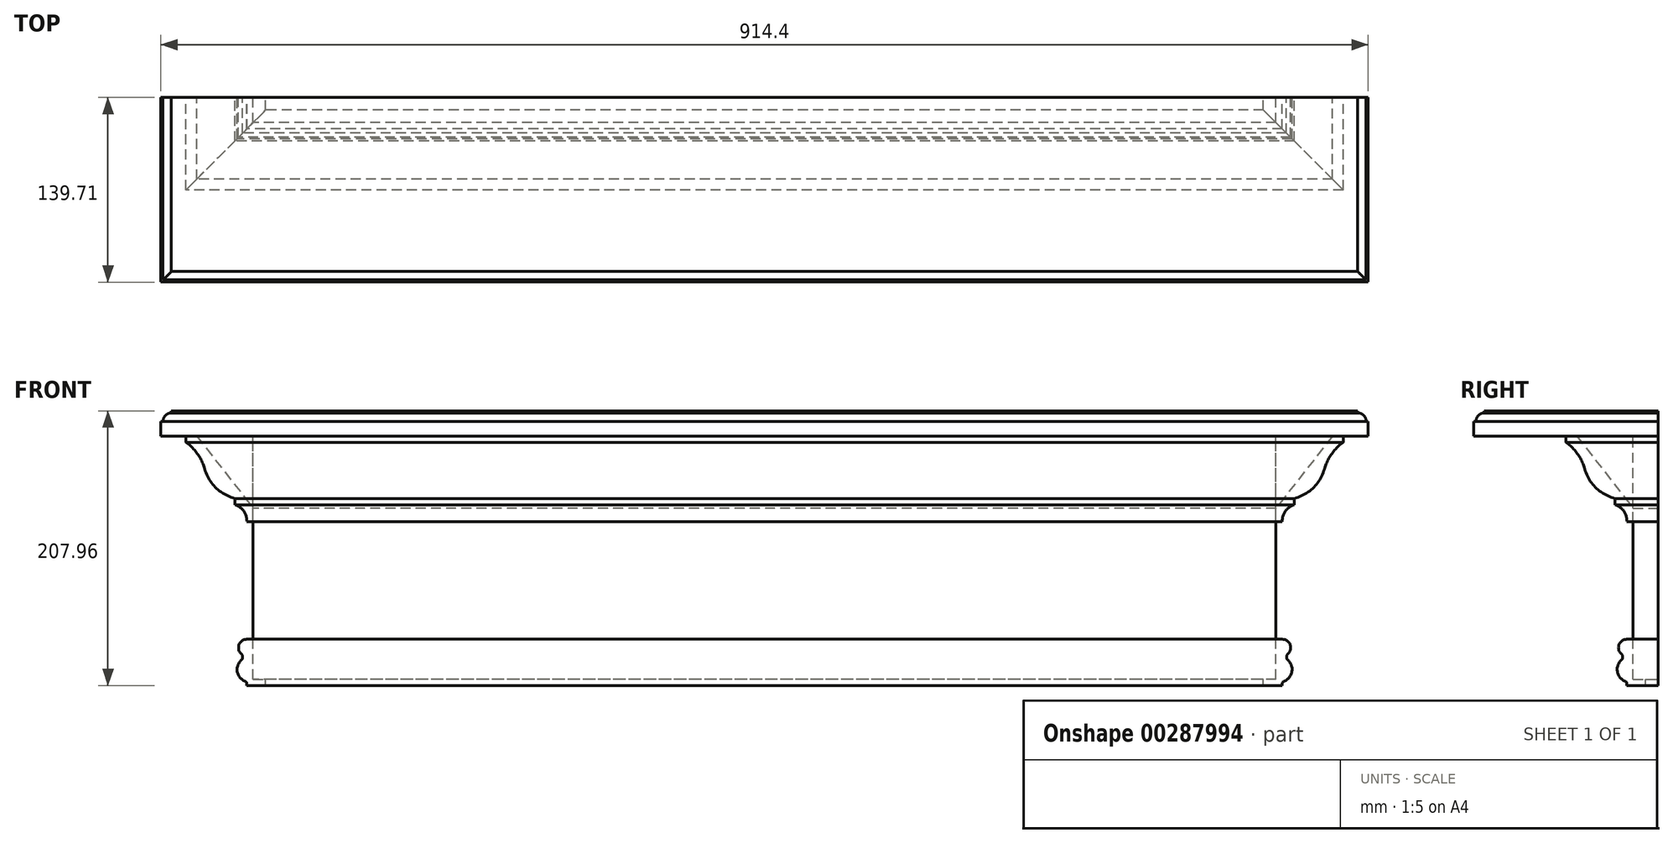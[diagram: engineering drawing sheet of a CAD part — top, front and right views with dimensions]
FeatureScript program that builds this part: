
annotation { "Feature Type Name" : "Feature", "Feature Type Description" : "" }
export const myFeature = defineFeature(function(context is Context, id is Id, definition is map)
    precondition{}
    {
        {
            var Q0;
            Q0=qCreatedBy(makeId("Right.planeOp"),FACE);
            var sketch = newSketch(context, id + "F0", { "sketchPlane" : qUnion([Q0])});
            skLineSegment(sketch, "E0.bottom", {"start": v(-9.52, -92.08) * mm, "end": v(9.52, -92.08) * mm});
            skLineSegment(sketch, "E0.top", {"start": v(-9.52, 92.08) * mm, "end": v(9.52, 92.08) * mm});
            skLineSegment(sketch, "E0.left", {"start": v(-9.52, -92.07) * mm, "end": v(-9.52, 92.08) * mm});
            skLineSegment(sketch, "E0.right", {"start": v(9.52, -92.07) * mm, "end": v(9.52, 92.08) * mm});
            skPoint(sketch, "E0.middle", {"position": v(0, 0) * mm});
            skLineSegment(sketch, "E1.bottom", {"start": v(9.52, 92.08) * mm, "end": v(-130.18, 92.08) * mm});
            skLineSegment(sketch, "E1.top", {"start": v(9.53, 111.13) * mm, "end": v(-130.18, 111.12) * mm});
            skLineSegment(sketch, "E1.left", {"start": v(9.53, 92.08) * mm, "end": v(9.53, 111.13) * mm});
            skLineSegment(sketch, "E1.right", {"start": v(-130.18, 92.08) * mm, "end": v(-130.18, 111.12) * mm});
            skLineSegment(sketch, "E2", {"start": v(-52.29, 92.08) * mm, "end": v(-9.52, 37.34) * mm});
            skLineSegment(sketch, "E3", {"start": v(-9.52, 27.02) * mm, "end": v(-60.35, 92.08) * mm, "construction": true});
            skLineSegment(sketch, "E4", {"start": v(-9.52, 27.02) * mm, "end": v(-14.29, 27.02) * mm});
            skArc(sketch, "E5", {"start": v(-14.29, 27.02) * mm, "mid": v(-16.56, 35.12) * mm, "end": v(-23.4, 40.02) * mm});
            skLineSegment(sketch, "E6", {"start": v(-23.4, 40.02) * mm, "end": v(-23.4, 44.79) * mm});
            skArc(sketch, "E7", {"start": v(-46.16, 66.92) * mm, "mid": v(-37.75, 52.8) * mm, "end": v(-23.4, 44.79) * mm});
            skArc(sketch, "E8", {"start": v(-46.16, 66.92) * mm, "mid": v(-51.55, 78.3) * mm, "end": v(-60.35, 87.31) * mm});
            skLineSegment(sketch, "E9", {"start": v(-60.35, 87.31) * mm, "end": v(-60.35, 92.08) * mm});
            skLineSegment(sketch, "E10", {"start": v(-9.52, -61.86) * mm, "end": v(-14.29, -61.86) * mm});
            skArc(sketch, "E11", {"start": v(-14.29, -61.86) * mm, "mid": v(-20.22, -65.94) * mm, "end": v(-18.52, -72.94) * mm});
            skArc(sketch, "E12", {"start": v(-18.52, -77.67) * mm, "mid": v(-17.46, -75.3) * mm, "end": v(-18.52, -72.94) * mm});
            skArc(sketch, "E13", {"start": v(-18.52, -77.67) * mm, "mid": v(-21.52, -86.62) * mm, "end": v(-15.35, -93.75) * mm});
            skLineSegment(sketch, "E14", {"start": v(0, -96.84) * mm, "end": v(0, -92.08) * mm});
            skLineSegment(sketch, "E15", {"start": v(-14.29, -95.25) * mm, "end": v(-14.29, -96.84) * mm});
            skLineSegment(sketch, "E16", {"start": v(-14.29, -96.84) * mm, "end": v(0, -96.84) * mm});
            skPoint(sketch, "E17.visualSharp", {"position": v(-14.29, -94.06) * mm});
            skArc(sketch, "E17.filletArc", {"start": v(-14.29, -95.25) * mm, "mid": v(-14.58, -94.33) * mm, "end": v(-15.35, -93.75) * mm});
            skLineSegment(sketch, "E18", {"start": v(-122.24, 111.12) * mm, "end": v(-122.24, 109.54) * mm});
            skArc(sketch, "E19", {"start": v(-122.24, 109.54) * mm, "mid": v(-126.73, 107.68) * mm, "end": v(-128.59, 103.19) * mm});
            skLineSegment(sketch, "E20", {"start": v(-128.59, 103.19) * mm, "end": v(-130.17, 103.19) * mm});
            skSolve(sketch);
        }
        {
            var Q0;
            Q0=qCreatedBy(makeId("Front.planeOp"),FACE);
            var sketch = newSketch(context, id + "F1", { "sketchPlane" : qUnion([Q0])});
            skLineSegment(sketch, "E21", {"start": v(-387.35, 0) * mm, "end": v(387.35, 0) * mm});
            skLineSegment(sketch, "E22", {"start": v(-387.35, 0) * mm, "end": v(-457.2, 0) * mm});
            skLineSegment(sketch, "E23", {"start": v(387.35, 0) * mm, "end": v(457.2, 0) * mm});
            skSolve(sketch);
        }
        {
            var Q0;
            {var subQ7=sQuery(id+"F0.wireOp",EDGE,"E1.left");Q0=makeQuery(id+"F0.imprint","IMPRINT",FACE,{"disambiguationData":[TD([[makeQuery(id+"F0.imprint","IMPRINT",EDGE,{"derivedFrom":subQ7}),1.0]])]});}
            var Q1;
            Q1=sQuery(id+"F1.wireOp",VERTEX,"E23.end");
            extrude(context, id + "F2", {"entities" : qUnion([Q0]), "endBound" : BoundingType.UP_TO_VERTEX, "endBoundEntityVertex" : qUnion([Q1]), "depth" : 25.4 * mm});
        }
        {
            var Q0;
            Q0=makeQuery(id+"F2.opExtrude","SWEPT_FACE",FACE,{"disambiguationData":[OSD([sQuery(id+"F0.wireOp",EDGE,"E1.left")])]});
            var sketch = newSketch(context, id + "F3", { "sketchPlane" : qUnion([Q0])});
            skLineSegment(sketch, "E24", {"start": v(-449.26, 111.13) * mm, "end": v(-449.26, 109.54) * mm});
            skLineSegment(sketch, "E25", {"start": v(-457.2, 103.19) * mm, "end": v(-455.61, 103.19) * mm});
            skArc(sketch, "E26", {"start": v(-449.26, 109.54) * mm, "mid": v(-453.75, 107.68) * mm, "end": v(-455.61, 103.19) * mm});
            skLineSegment(sketch, "E27", {"start": v(-457.2, 103.19) * mm, "end": v(-457.2, 111.13) * mm});
            skLineSegment(sketch, "E28", {"start": v(-457.2, 111.13) * mm, "end": v(-449.26, 111.13) * mm});
            skSolve(sketch);
        }
        {
            var Q0;
            Q0 = qSketchRegion(id + "F3", true);
            extrude(context, id + "F4", {"entities" : qUnion([Q0]), "operationType" : NewBodyOperationType.REMOVE, "endBound" : BoundingType.THROUGH_ALL, "oppositeDirection" : true, "depth" : 25.4 * mm});
        }
        {
            var Q0;
            Q0=makeQuery(id+"F2.opExtrude","SWEPT_BODY",BODY,{"disambiguationData":[OSD([sQuery(id+"F0.wireOp",EDGE,"E1.bottom"),sQuery(id+"F0.wireOp",EDGE,"E1.top"),sQuery(id+"F0.wireOp",EDGE,"E1.left"),sQuery(id+"F0.wireOp",EDGE,"E1.right"),sQuery(id+"F0.wireOp",EDGE,"E18"),sQuery(id+"F0.wireOp",EDGE,"E19"),sQuery(id+"F0.wireOp",EDGE,"E20")])]});
            var Q1;
            Q1=qCreatedBy(makeId("Right.planeOp"),FACE);
            mirror(context, id + "F5", {"operationType" : NewBodyOperationType.ADD, "entities" : qUnion([Q0]), "mirrorPlane" : qUnion([Q1])});
        }
        {
            var Q0;
            {var subQ5=sQuery(id+"F0.wireOp",EDGE,"E0.bottom");Q0=makeQuery(id+"F0.imprint","IMPRINT",FACE,{"disambiguationData":[TD([[makeQuery(id+"F0.imprint","IMPRINT",EDGE,{"derivedFrom":subQ5}),1.0]])]});}
            var Q1;
            Q1=sQuery(id+"F1.wireOp",VERTEX,"E23.start");
            extrude(context, id + "F6", {"entities" : qUnion([Q0]), "endBound" : BoundingType.UP_TO_VERTEX, "endBoundEntityVertex" : qUnion([Q1]), "depth" : 25.4 * mm});
        }
        {
            var Q0;
            Q0=makeQuery(id+"F6.opExtrude","SWEPT_BODY",BODY,{"disambiguationData":[OSD([sQuery(id+"F0.wireOp",EDGE,"E0.bottom"),sQuery(id+"F0.wireOp",EDGE,"E0.left"),sQuery(id+"F0.wireOp",EDGE,"E0.right"),sQuery(id+"F0.wireOp",EDGE,"E1.bottom")])]});
            var Q1;
            Q1=qCreatedBy(makeId("Right.planeOp"),FACE);
            mirror(context, id + "F7", {"operationType" : NewBodyOperationType.ADD, "entities" : qUnion([Q0]), "mirrorPlane" : qUnion([Q1])});
        }
        {
            var Q0;
            {var subQ0=sQuery(id+"F0.wireOp",EDGE,"E2");Q0=makeQuery(id+"F0.imprint","IMPRINT",FACE,{"disambiguationData":[TD([[makeQuery(id+"F0.imprint","IMPRINT",EDGE,{"derivedFrom":subQ0}),-1.0]])]});}
            var Q1;
            Q1=sQuery(id+"F1.wireOp",VERTEX,"E23.end");
            extrude(context, id + "F8", {"entities" : qUnion([Q0]), "endBound" : BoundingType.UP_TO_VERTEX, "endBoundEntityVertex" : qUnion([Q1]), "depth" : 25.4 * mm});
        }
        {
            var Q0;
            Q0=makeQuery(id+"F6.opExtrude","CAP_EDGE",EDGE,{"disambiguationData":[OSD([sQuery(id+"F0.wireOp",EDGE,"E0.left")])],"isStart":false});
            var Q1;
            Q1=makeQuery(id+"F6.opExtrude","CAP_FACE",FACE,{"disambiguationData":[OSD([sQuery(id+"F0.wireOp",EDGE,"E0.bottom"),sQuery(id+"F0.wireOp",EDGE,"E0.left"),sQuery(id+"F0.wireOp",EDGE,"E0.right"),sQuery(id+"F0.wireOp",EDGE,"E1.bottom")])],"isStart":false});
            cPlane(context, id + "F9", {"entities" : qUnion([Q0, Q1]), "cplaneType" : CPlaneType.LINE_ANGLE, "offset" : 25.4 * mm, "angle" : 45 * degree, "width" : 152.4 * mm, "height" : 152.4 * mm});
        }
        {
            var Q0;
            Q0=makeQuery(id+"F8.opExtrude","CAP_FACE",FACE,{"disambiguationData":[OSD([sQuery(id+"F0.wireOp",EDGE,"E0.left"),sQuery(id+"F0.wireOp",EDGE,"E1.bottom"),sQuery(id+"F0.wireOp",EDGE,"E2"),sQuery(id+"F0.wireOp",EDGE,"E4"),sQuery(id+"F0.wireOp",EDGE,"E5"),sQuery(id+"F0.wireOp",EDGE,"E6"),sQuery(id+"F0.wireOp",EDGE,"E7"),sQuery(id+"F0.wireOp",EDGE,"E8"),sQuery(id+"F0.wireOp",EDGE,"E9")])],"isStart":false});
            var Q1;
            Q1=qCreatedBy(id+"F9.planeOp",FACE);
            extrude(context, id + "F10", {"entities" : qUnion([Q0]), "operationType" : NewBodyOperationType.REMOVE, "endBound" : BoundingType.UP_TO_SURFACE, "oppositeDirection" : true, "endBoundEntityFace" : qUnion([Q1]), "depth" : 25.4 * mm});
        }
        {
            var Q0;
            Q0=makeQuery(id+"F8.opExtrude","SWEPT_BODY",BODY,{"disambiguationData":[OSD([sQuery(id+"F0.wireOp",EDGE,"E0.left"),sQuery(id+"F0.wireOp",EDGE,"E1.bottom"),sQuery(id+"F0.wireOp",EDGE,"E2"),sQuery(id+"F0.wireOp",EDGE,"E4"),sQuery(id+"F0.wireOp",EDGE,"E5"),sQuery(id+"F0.wireOp",EDGE,"E6"),sQuery(id+"F0.wireOp",EDGE,"E7"),sQuery(id+"F0.wireOp",EDGE,"E8"),sQuery(id+"F0.wireOp",EDGE,"E9")])]});
            var Q1;
            Q1=qCreatedBy(makeId("Right.planeOp"),FACE);
            mirror(context, id + "F11", {"operationType" : NewBodyOperationType.ADD, "entities" : qUnion([Q0]), "mirrorPlane" : qUnion([Q1])});
        }
        {
            var Q0;
            {var subQ0=makeQuery(id+"F6.opExtrude","SWEPT_FACE",FACE,{"disambiguationData":[OSD([sQuery(id+"F0.wireOp",EDGE,"E0.right")])]});Q0=makeQuery(id+"F7.boolean.opBoolean","MERGE",FACE,{"derivedFrom":[subQ0,makeQuery(id+"F7.opPattern","COPY",FACE,{"derivedFrom":subQ0,"instanceName":"1"})]});}
            var sketch = newSketch(context, id + "F12", { "sketchPlane" : qUnion([Q0])});
            skLineSegment(sketch, "E29.0", {"start": v(-430.11, 92.07) * mm, "end": v(-387.35, 37.34) * mm});
            skLineSegment(sketch, "E30.0", {"start": v(-438.17, 87.31) * mm, "end": v(-438.17, 92.08) * mm});
            skArc(sketch, "E31.0", {"start": v(-423.99, 66.92) * mm, "mid": v(-429.37, 78.3) * mm, "end": v(-438.17, 87.31) * mm});
            skArc(sketch, "E32.0", {"start": v(-423.99, 66.92) * mm, "mid": v(-415.57, 52.8) * mm, "end": v(-401.23, 44.79) * mm});
            skLineSegment(sketch, "E33.0", {"start": v(-401.23, 40.02) * mm, "end": v(-401.23, 44.79) * mm});
            skArc(sketch, "E34.0", {"start": v(-392.11, 27.02) * mm, "mid": v(-394.39, 35.12) * mm, "end": v(-401.23, 40.02) * mm});
            skLineSegment(sketch, "E35.0", {"start": v(-387.35, 27.02) * mm, "end": v(-392.11, 27.02) * mm});
            skLineSegment(sketch, "E36", {"start": v(-387.35, 27.02) * mm, "end": v(-387.35, 37.34) * mm});
            skLineSegment(sketch, "E37", {"start": v(-438.17, 92.08) * mm, "end": v(-430.11, 92.08) * mm});
            skSolve(sketch);
        }
        {
            var Q0;
            Q0 = qSketchRegion(id + "F12", true);
            var Q1;
            Q1=makeQuery(id+"F10.boolean.opBoolean","COPY",FACE,{"derivedFrom":makeQuery(id+"F10.opExtrude","CAP_FACE",FACE,{"disambiguationData":[OSD([sQuery(id+"F0.wireOp",EDGE,"E0.left"),sQuery(id+"F0.wireOp",EDGE,"E1.bottom"),sQuery(id+"F0.wireOp",EDGE,"E2"),sQuery(id+"F0.wireOp",EDGE,"E4"),sQuery(id+"F0.wireOp",EDGE,"E5"),sQuery(id+"F0.wireOp",EDGE,"E6"),sQuery(id+"F0.wireOp",EDGE,"E7"),sQuery(id+"F0.wireOp",EDGE,"E8"),sQuery(id+"F0.wireOp",EDGE,"E9")])],"isStart":false})});
            extrude(context, id + "F13", {"entities" : qUnion([Q0]), "endBound" : BoundingType.UP_TO_SURFACE, "oppositeDirection" : true, "endBoundEntityFace" : qUnion([Q1]), "depth" : 25.4 * mm});
        }
        {
            var Q0;
            {var subQ0=sQuery(id+"F0.wireOp",EDGE,"E10");Q0=makeQuery(id+"F0.imprint","IMPRINT",FACE,{"disambiguationData":[TD([[makeQuery(id+"F0.imprint","IMPRINT",EDGE,{"derivedFrom":subQ0}),1.0]])]});}
            var Q1;
            Q1=makeQuery(id+"F6.opExtrude","CAP_FACE",FACE,{"disambiguationData":[OSD([sQuery(id+"F0.wireOp",EDGE,"E0.bottom"),sQuery(id+"F0.wireOp",EDGE,"E0.left"),sQuery(id+"F0.wireOp",EDGE,"E0.right"),sQuery(id+"F0.wireOp",EDGE,"E1.bottom")])],"isStart":false});
            var Q2;
            Q2=sQuery(id+"F1.wireOp",VERTEX,"E23.end");
            extrude(context, id + "F14", {"entities" : qUnion([Q0]), "endBound" : BoundingType.UP_TO_VERTEX, "endBoundEntityFace" : qUnion([Q1]), "endBoundEntityVertex" : qUnion([Q2]), "depth" : 25.4 * mm});
        }
        {
            var Q0;
            Q0=makeQuery(id+"F14.opExtrude","CAP_FACE",FACE,{"disambiguationData":[OSD([sQuery(id+"F0.wireOp",EDGE,"E0.bottom"),sQuery(id+"F0.wireOp",EDGE,"E0.left"),sQuery(id+"F0.wireOp",EDGE,"E10"),sQuery(id+"F0.wireOp",EDGE,"E11"),sQuery(id+"F0.wireOp",EDGE,"E12"),sQuery(id+"F0.wireOp",EDGE,"E13"),sQuery(id+"F0.wireOp",EDGE,"E14"),sQuery(id+"F0.wireOp",EDGE,"E15"),sQuery(id+"F0.wireOp",EDGE,"E16"),sQuery(id+"F0.wireOp",EDGE,"E17.filletArc")])],"isStart":false});
            var Q1;
            Q1=qCreatedBy(id+"F9.planeOp",FACE);
            extrude(context, id + "F15", {"entities" : qUnion([Q0]), "operationType" : NewBodyOperationType.REMOVE, "endBound" : BoundingType.UP_TO_SURFACE, "oppositeDirection" : true, "endBoundEntityFace" : qUnion([Q1]), "depth" : 25.4 * mm});
        }
        {
            var Q0;
            Q0=makeQuery(id+"F14.opExtrude","SWEPT_BODY",BODY,{"disambiguationData":[OSD([sQuery(id+"F0.wireOp",EDGE,"E0.bottom"),sQuery(id+"F0.wireOp",EDGE,"E0.left"),sQuery(id+"F0.wireOp",EDGE,"E10"),sQuery(id+"F0.wireOp",EDGE,"E11"),sQuery(id+"F0.wireOp",EDGE,"E12"),sQuery(id+"F0.wireOp",EDGE,"E13"),sQuery(id+"F0.wireOp",EDGE,"E14"),sQuery(id+"F0.wireOp",EDGE,"E15"),sQuery(id+"F0.wireOp",EDGE,"E16"),sQuery(id+"F0.wireOp",EDGE,"E17.filletArc")])]});
            var Q1;
            Q1=qCreatedBy(makeId("Right.planeOp"),FACE);
            mirror(context, id + "F16", {"operationType" : NewBodyOperationType.ADD, "entities" : qUnion([Q0]), "mirrorPlane" : qUnion([Q1])});
        }
        {
            var Q0;
            {var subQ0=makeQuery(id+"F6.opExtrude","SWEPT_FACE",FACE,{"disambiguationData":[OSD([sQuery(id+"F0.wireOp",EDGE,"E0.right")])]});Q0=makeQuery(id+"F7.boolean.opBoolean","MERGE",FACE,{"derivedFrom":[subQ0,makeQuery(id+"F7.opPattern","COPY",FACE,{"derivedFrom":subQ0,"instanceName":"1"})]});}
            var sketch = newSketch(context, id + "F17", { "sketchPlane" : qUnion([Q0])});
            skLineSegment(sketch, "E38.0", {"start": v(-387.35, -61.86) * mm, "end": v(-392.11, -61.86) * mm});
            skArc(sketch, "E39.0", {"start": v(-392.11, -61.86) * mm, "mid": v(-398.04, -65.94) * mm, "end": v(-396.35, -72.94) * mm});
            skArc(sketch, "E40.0", {"start": v(-396.35, -77.67) * mm, "mid": v(-395.29, -75.3) * mm, "end": v(-396.35, -72.94) * mm});
            skArc(sketch, "E41.0", {"start": v(-396.35, -77.67) * mm, "mid": v(-399.34, -86.62) * mm, "end": v(-393.17, -93.75) * mm});
            skArc(sketch, "E42.0", {"start": v(-392.11, -95.25) * mm, "mid": v(-392.4, -94.33) * mm, "end": v(-393.17, -93.75) * mm});
            skLineSegment(sketch, "E43.0", {"start": v(-392.11, -95.25) * mm, "end": v(-392.11, -96.84) * mm});
            skLineSegment(sketch, "E44.0", {"start": v(-392.11, -96.84) * mm, "end": v(-377.83, -96.84) * mm});
            skLineSegment(sketch, "E45.0", {"start": v(-377.83, -96.84) * mm, "end": v(-377.83, -92.08) * mm});
            skLineSegment(sketch, "E46", {"start": v(-377.83, -92.07) * mm, "end": v(-387.35, -92.07) * mm});
            skLineSegment(sketch, "E47", {"start": v(-387.35, -92.08) * mm, "end": v(-387.35, -61.86) * mm});
            skSolve(sketch);
        }
        {
            var Q0;
            Q0 = qSketchRegion(id + "F17", true);
            var Q1;
            Q1=makeQuery(id+"F15.boolean.opBoolean","COPY",FACE,{"derivedFrom":makeQuery(id+"F15.opExtrude","CAP_FACE",FACE,{"disambiguationData":[OSD([sQuery(id+"F0.wireOp",EDGE,"E0.bottom"),sQuery(id+"F0.wireOp",EDGE,"E0.left"),sQuery(id+"F0.wireOp",EDGE,"E10"),sQuery(id+"F0.wireOp",EDGE,"E11"),sQuery(id+"F0.wireOp",EDGE,"E12"),sQuery(id+"F0.wireOp",EDGE,"E13"),sQuery(id+"F0.wireOp",EDGE,"E14"),sQuery(id+"F0.wireOp",EDGE,"E15"),sQuery(id+"F0.wireOp",EDGE,"E16"),sQuery(id+"F0.wireOp",EDGE,"E17.filletArc")])],"isStart":false})});
            extrude(context, id + "F18", {"entities" : qUnion([Q0]), "endBound" : BoundingType.UP_TO_SURFACE, "oppositeDirection" : true, "endBoundEntityFace" : qUnion([Q1]), "depth" : 25.4 * mm});
        }
        {
            var Q0;
            Q0=makeQuery(id+"F13.opExtrude","SWEPT_BODY",BODY,{"disambiguationData":[OSD([sQuery(id+"F12.wireOp",EDGE,"E29.0"),sQuery(id+"F12.wireOp",EDGE,"E30.0"),sQuery(id+"F12.wireOp",EDGE,"E31.0"),sQuery(id+"F12.wireOp",EDGE,"E32.0"),sQuery(id+"F12.wireOp",EDGE,"E33.0"),sQuery(id+"F12.wireOp",EDGE,"E34.0"),sQuery(id+"F12.wireOp",EDGE,"E35.0"),sQuery(id+"F12.wireOp",EDGE,"E36"),sQuery(id+"F12.wireOp",EDGE,"E37")])]});
            var Q1;
            Q1=makeQuery(id+"F18.opExtrude","SWEPT_BODY",BODY,{"disambiguationData":[OSD([sQuery(id+"F17.wireOp",EDGE,"E38.0"),sQuery(id+"F17.wireOp",EDGE,"E39.0"),sQuery(id+"F17.wireOp",EDGE,"E40.0"),sQuery(id+"F17.wireOp",EDGE,"E41.0"),sQuery(id+"F17.wireOp",EDGE,"E42.0"),sQuery(id+"F17.wireOp",EDGE,"E43.0"),sQuery(id+"F17.wireOp",EDGE,"E44.0"),sQuery(id+"F17.wireOp",EDGE,"E45.0"),sQuery(id+"F17.wireOp",EDGE,"E46"),sQuery(id+"F17.wireOp",EDGE,"E47")])]});
            var Q2;
            Q2=qCreatedBy(makeId("Right.planeOp"),FACE);
            mirror(context, id + "F19", {"entities" : qUnion([Q0, Q1]), "mirrorPlane" : qUnion([Q2])});
        }
    });
